# Revit family: Haworth_Luxor_Cabinet_19
name_source: partatom
category: Furniture
revit_build: Autodesk Revit 2018 (Build: 20170223_1515(x64)
units: mm (PartAtom-declared; Revit-internal decimal feet)

## family parameters
Always vertical = Yes
Cut with Voids When Loaded = No
OmniClass Number = 23.40.20.00
OmniClass Title = General Furniture and Specialties
Room Calculation Point = No
Shared = No
Work Plane-Based = No

## types (2) — shared parameters
Assembly Code = E2020200
Description = Haworth Luxor Cabinet 19
Manufacturer = Haworth
Model = HCCE-LX
Size = Verify Final Dim. w/ Haworth
URL = http://www.haworth.com
URL - Product = https://www.haworth.com
Version = 3
Warranty = http://www.haworth.com

## per-type parameters (varying)
| type | Door/Open & Drawer/Door | Open/Four Drawers |
| HCCE-LX - Door/Open & Drawer/Door - 106w 26h | Yes | No |
| HCCE-LX - Open/Four Drawers - 106w 26h | No | Yes |

## geometry (parser evidence)
native form markers: Blend x4, Sweep x9
no freeform markers — native parametric forms only
